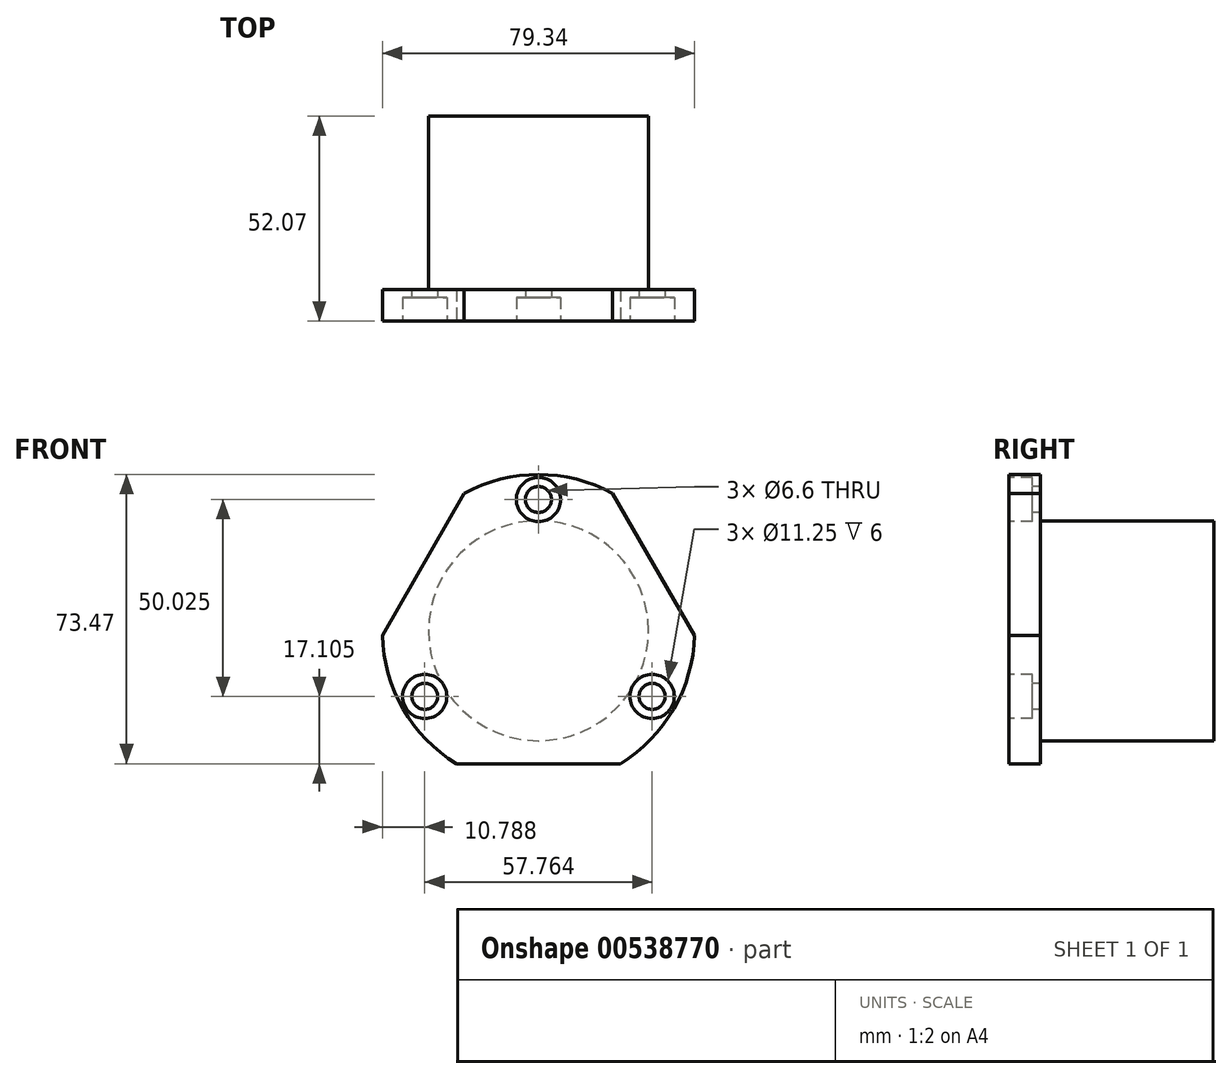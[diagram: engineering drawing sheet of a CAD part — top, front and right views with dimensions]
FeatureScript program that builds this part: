
annotation { "Feature Type Name" : "Feature", "Feature Type Description" : "" }
export const myFeature = defineFeature(function(context is Context, id is Id, definition is map)
    precondition{}
    {
        {
            var Q0;
            Q0=qCreatedBy(makeId("Right.planeOp"),FACE);
            var sketch = newSketch(context, id + "F0", { "sketchPlane" : qUnion([Q0])});
            skLineSegment(sketch, "E0", {"start": v(0, 0) * mm, "end": v(0, 27.94) * mm});
            skLineSegment(sketch, "E1", {"start": v(0, 27.94) * mm, "end": v(-44.07, 27.94) * mm});
            skLineSegment(sketch, "E2", {"start": v(-44.07, 27.94) * mm, "end": v(-44.07, 39.69) * mm});
            skLineSegment(sketch, "E3", {"start": v(-44.07, 39.69) * mm, "end": v(-52.07, 39.69) * mm});
            skLineSegment(sketch, "E4", {"start": v(-52.07, 39.69) * mm, "end": v(-52.07, 0) * mm});
            skLineSegment(sketch, "E5", {"start": v(-52.07, 0) * mm, "end": v(0, 0) * mm});
            skLineSegment(sketch, "E6", {"start": v(-87.65, 0) * mm, "end": v(17.78, 0) * mm, "construction": true});
            skSolve(sketch);
        }
        {
            var Q0;
            Q0=makeQuery(id+"F0.imprint","IMPRINT",FACE,{"disambiguationData":[TD([[makeQuery(id+"F0.imprint","IMPRINT",EDGE,{"derivedFrom":sQuery(id+"F0.wireOp",EDGE,"E0")}),1.0]])]});
            var Q1;
            Q1=sQuery(id+"F0.wireOp",EDGE,"E6");
            revolve(context, id + "F1", {"entities" : qUnion([Q0]), "axis" : qUnion([Q1]), "revolveType" : RevolveType.FULL});
        }
        {
            var Q0;
            Q0=makeQuery(id+"F1.opRevolve","SWEPT_FACE",FACE,{"disambiguationData":[OSD([sQuery(id+"F0.wireOp",EDGE,"E4")])]});
            var sketch = newSketch(context, id + "F2", { "sketchPlane" : qUnion([Q0])});
            skCircle(sketch, "E7", {"center": v(0, 33.35) * mm, "radius": 3.5 * mm});
            skCircle(sketch, "E8.1.0", {"center": v(-28.88, -16.68) * mm, "radius": 3.5 * mm});
            skCircle(sketch, "E8.2.0", {"center": v(28.88, -16.68) * mm, "radius": 3.5 * mm});
            skPoint(sketch, "E8.center", {"position": v(0, 0) * mm});
            skSolve(sketch);
        }
        {
            var Q0;
            Q0=sQuery(id+"F2.wireOp",VERTEX,"E7.center");
            var Q1;
            Q1=sQuery(id+"F2.wireOp",VERTEX,"E8.1.0.center");
            var Q2;
            Q2=sQuery(id+"F2.wireOp",VERTEX,"E8.2.0.center");
            var Q3;
            Q3=makeQuery(id+"F1.opRevolve","SWEPT_BODY",BODY,{"disambiguationData":[OSD([sQuery(id+"F0.wireOp",EDGE,"E0"),sQuery(id+"F0.wireOp",EDGE,"E1"),sQuery(id+"F0.wireOp",EDGE,"E2"),sQuery(id+"F0.wireOp",EDGE,"E3"),sQuery(id+"F0.wireOp",EDGE,"E4"),sQuery(id+"F0.wireOp",EDGE,"E5")])]});
            hole(context, id + "F3", {"style" : HoleStyle.C_BORE, "endStyle" : HoleEndStyle.THROUGH, "standardTappedOrClearance" : lookupTablePath({ "standard" : "ISO", "fit" : "Normal", "size" : "M6", "type" : "Clearance" }), "standardBlindInLast" : lookupTablePath({ "fit" : "Standard", "standard" : "ISO", "size" : "M6", "type" : "Clearance" }), "holeDiameter" : 6.6 * mm, "cBoreDiameter" : 11.25 * mm, "cBoreDepth" : 6 * mm, "isTappedThrough" : true, "tappedDepth" : 12.7 * mm, "tapClearance" : 3, "locations" : qUnion([Q0, Q1, Q2]), "scope" : qUnion([Q3])});
        }
        {
            var Q0;
            Q0=makeQuery(id+"F1.opRevolve","SWEPT_FACE",FACE,{"disambiguationData":[OSD([sQuery(id+"F0.wireOp",EDGE,"E4")])]});
            var sketch = newSketch(context, id + "F4", { "sketchPlane" : qUnion([Q0])});
            skLineSegment(sketch, "E9", {"start": v(18.84, 34.93) * mm, "end": v(39.67, -1.15) * mm});
            skArc(sketch, "E10", {"start": v(39.67, -1.15) * mm, "mid": v(34.37, 19.84) * mm, "end": v(18.84, 34.93) * mm});
            skLineSegment(sketch, "E11.1.0", {"start": v(-39.67, -1.15) * mm, "end": v(-18.84, 34.93) * mm});
            skLineSegment(sketch, "E11.2.0", {"start": v(20.83, -33.78) * mm, "end": v(-20.83, -33.78) * mm});
            skSolve(sketch);
        }
        {
            var Q0;
            Q0=makeQuery(id+"F4.imprint","IMPRINT",FACE,{"disambiguationData":[TD([[makeQuery(id+"F4.imprint","IMPRINT",EDGE,{"derivedFrom":sQuery(id+"F4.wireOp",EDGE,"E9")}),1.0]])]});
            var Q1;
            {var subQ0=sQuery(id+"F4.wireOp",EDGE,"E11.1.0");Q1=makeQuery(id+"F4.imprint","IMPRINT",FACE,{"disambiguationData":[TD([[makeQuery(id+"F4.imprint","IMPRINT",EDGE,{"derivedFrom":subQ0}),1.0]])]});}
            var Q2;
            {var subQ0=sQuery(id+"F4.wireOp",EDGE,"E11.2.0");Q2=makeQuery(id+"F4.imprint","IMPRINT",FACE,{"disambiguationData":[TD([[makeQuery(id+"F4.imprint","IMPRINT",EDGE,{"derivedFrom":subQ0}),1.0]])]});}
            extrude(context, id + "F5", {"entities" : qUnion([Q0, Q1, Q2]), "operationType" : NewBodyOperationType.REMOVE, "endBound" : BoundingType.THROUGH_ALL, "oppositeDirection" : true, "depth" : 25.4 * mm, "offsetDistance" : 25.4 * mm});
        }
    });
